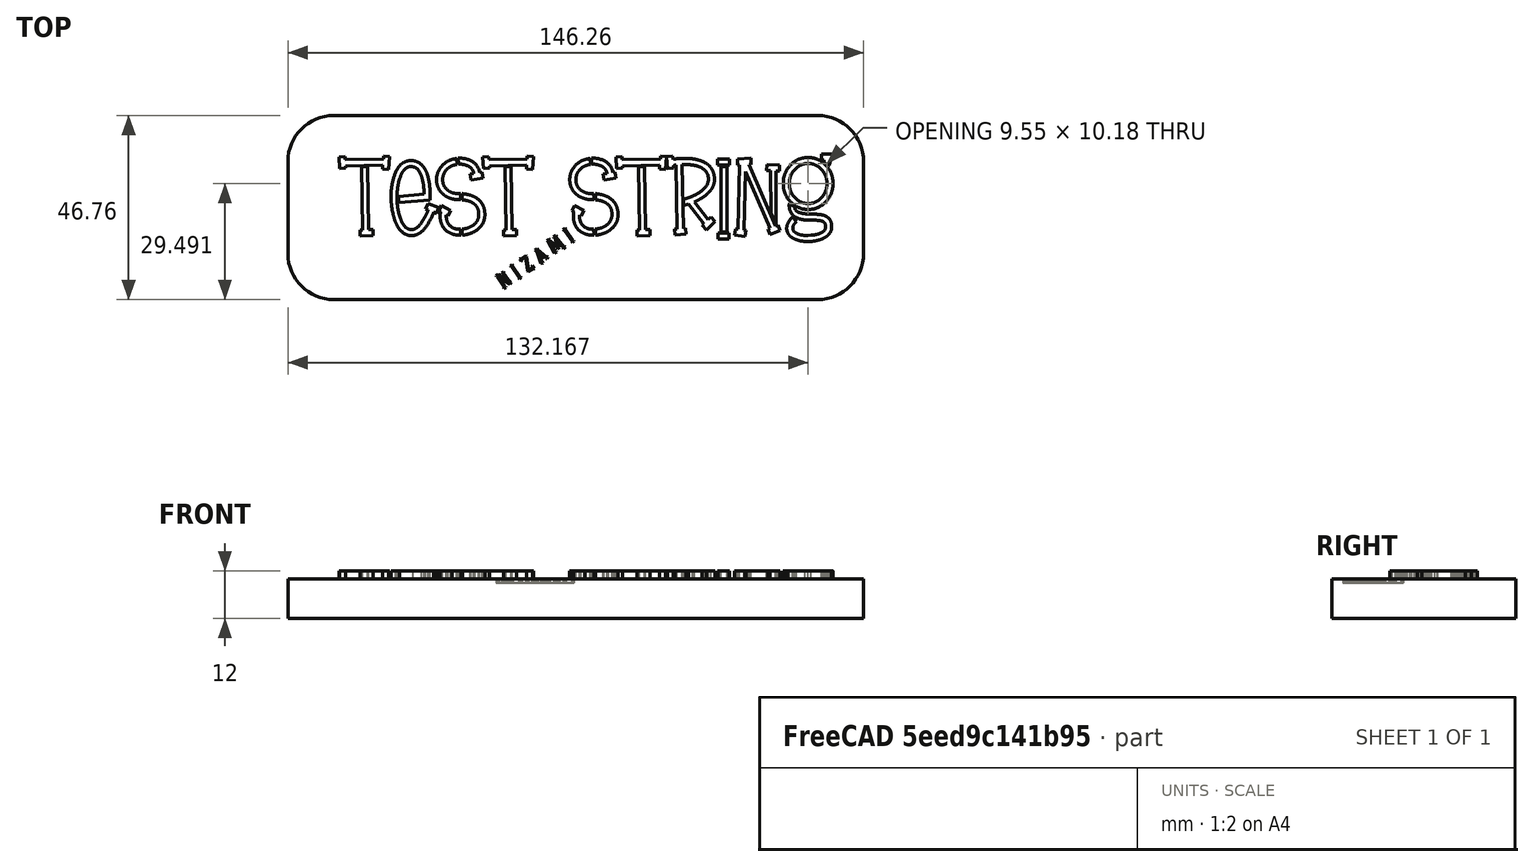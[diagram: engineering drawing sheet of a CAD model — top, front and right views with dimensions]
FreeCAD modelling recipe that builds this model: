
FCSTD DOCUMENT  (FreeCAD 0.21R33771 (Git))
Label: nadpisj
License: All rights reserved
LicenseURL: https://en.wikipedia.org/wiki/All_rights_reserved
objects: Part::Part2DObjectPython×3, Part::Extrusion×2, Sketcher::SketchObject×1, PartDesign::Pad×1, PartDesign::Body×1
note: 9 computed .brp shape members not serialized (recipe doc carries the construction recipe); baked Part::Feature solids carry a one-line shape summary decoded from their .brp

FEATURE [Sketcher::SketchObject] Sketch
  FullyConstrained = false
  MapMode = 5
  Support = -> [XY_Plane]
  sketch-geometry (10):
    g0: ArcOfCircle CenterX=-37.1464 CenterY=10.1913 CenterZ=0 NormalX=0 NormalY=0 NormalZ=1 AngleXU=0 Radius=11.6889 StartAngle=1.5708 EndAngle=3.14159
    g1: LineSegment StartX=-37.1464 StartY=21.8802 StartZ=0 EndX=85.7321 EndY=21.8802 EndZ=0
    g2: ArcOfCircle CenterX=85.7321 CenterY=10.1913 CenterZ=0 NormalX=0 NormalY=0 NormalZ=1 AngleXU=0 Radius=11.6889 StartAngle=1e-16 EndAngle=1.5708
    g3: LineSegment StartX=97.421 StartY=10.1913 StartZ=0 EndX=97.421 EndY=-13.1864 EndZ=0
    g4: ArcOfCircle CenterX=85.7321 CenterY=-13.1864 CenterZ=0 NormalX=0 NormalY=0 NormalZ=1 AngleXU=0 Radius=11.6889 StartAngle=4.71239 EndAngle=6.28319
    g5: LineSegment StartX=85.7321 StartY=-24.8752 StartZ=0 EndX=-37.1464 EndY=-24.8752 EndZ=0
    g6: ArcOfCircle CenterX=-37.1464 CenterY=-13.1864 CenterZ=0 NormalX=0 NormalY=0 NormalZ=1 AngleXU=0 Radius=11.6889 StartAngle=3.14159 EndAngle=4.71239
    g7: LineSegment StartX=-48.8353 StartY=-13.1864 StartZ=0 EndX=-48.8353 EndY=10.1913 EndZ=0
    g8: GeomPoint X=-48.8353 Y=21.8802 Z=0
    g9: GeomPoint X=97.421 Y=-24.8752 Z=0
  constraints (19):
    c: Tangent(g0,g1) = 1.5708
    c: Tangent(g1,g2) = 1.5708
    c: Tangent(g2,g3) = 1.5708
    c: Tangent(g3,g4) = 1.5708
    c: Tangent(g4,g5) = 1.5708
    c: Tangent(g5,g6) = 1.5708
    c: Tangent(g6,g7) = 1.5708
    c: Tangent(g7,g0) = 1.5708
    c: Horizontal(g1)
    c: Horizontal(g5)
    c: Vertical(g3)
    c: Vertical(g7)
    c: Equal(g0,g2)
    c: Equal(g2,g4)
    c: Equal(g4,g6)
    c: PointOnObject(g8,g1)
    c: PointOnObject(g8,g7)
    c: PointOnObject(g9,g3)
    c: PointOnObject(g9,g5)
FEATURE [PartDesign::Pad] Pad
  Direction = (0,0,1)
  Length = 10
  Length2 = 10
  Profile = -> Sketch
  ReferenceAxis = -> Sketch [N_Axis]
  Type = 0
FEATURE [PartDesign::Body] Body
  Group = -> [Sketch,Pad]
  Origin = -> Origin
  Tip = -> Pad
FEATURE [Part::Part2DObjectPython] ShapeString  # Draft 2D object (typed FeaturePython)
  FontFile = <userpath>/Downloads/brownie-stencil-font/BrownieStencil-8O8MJ.ttf
  MakeFace = true
  Placement = pos=(-35.11,-7.89,10) rot=(0,0,1;0rad)
  Size = 10
  String = Test string
  Tracking = 0
FEATURE [Part::Extrusion] Extrude004
  Base = -> ShapeString
  Dir = (0,0,1)
  DirMode = 2
  FaceMakerClass = Part::FaceMakerBullseye
  LengthFwd = 2
  LengthRev = 0
  Solid = false
  Symmetric = false
FEATURE [Part::Part2DObjectPython] ShapeString001  # Draft 2D object (typed FeaturePython)
  FontFile = <userpath>/Downloads/brownie-stencil-font/BrownieStencil-8O8MJ.ttf
  MakeFace = true
  Placement = pos=(6,-22,10) rot=(0,0,1;0.601964rad)
  Size = 2
  String = Nizami
  Tracking = 2
FEATURE [Part::Extrusion] Extrude
  Base = -> ShapeString001
  Dir = (0,0,1)
  DirMode = 2
  FaceMakerClass = Part::FaceMakerBullseye
  LengthFwd = 1
  LengthRev = 0
  Reversed = true
  Solid = false
  Symmetric = false
FEATURE [Part::Part2DObjectPython] ShapeString002  # Draft 2D object (typed FeaturePython)
  FontFile = <userpath>/Downloads/brownie-stencil-font/BrownieStencil-8O8MJ.ttf
  MakeFace = true
  Placement = pos=(33.42,-14.35,10) rot=(0,0,1;0.360506rad)
  Size = 3
  String = A
  Tracking = 0
